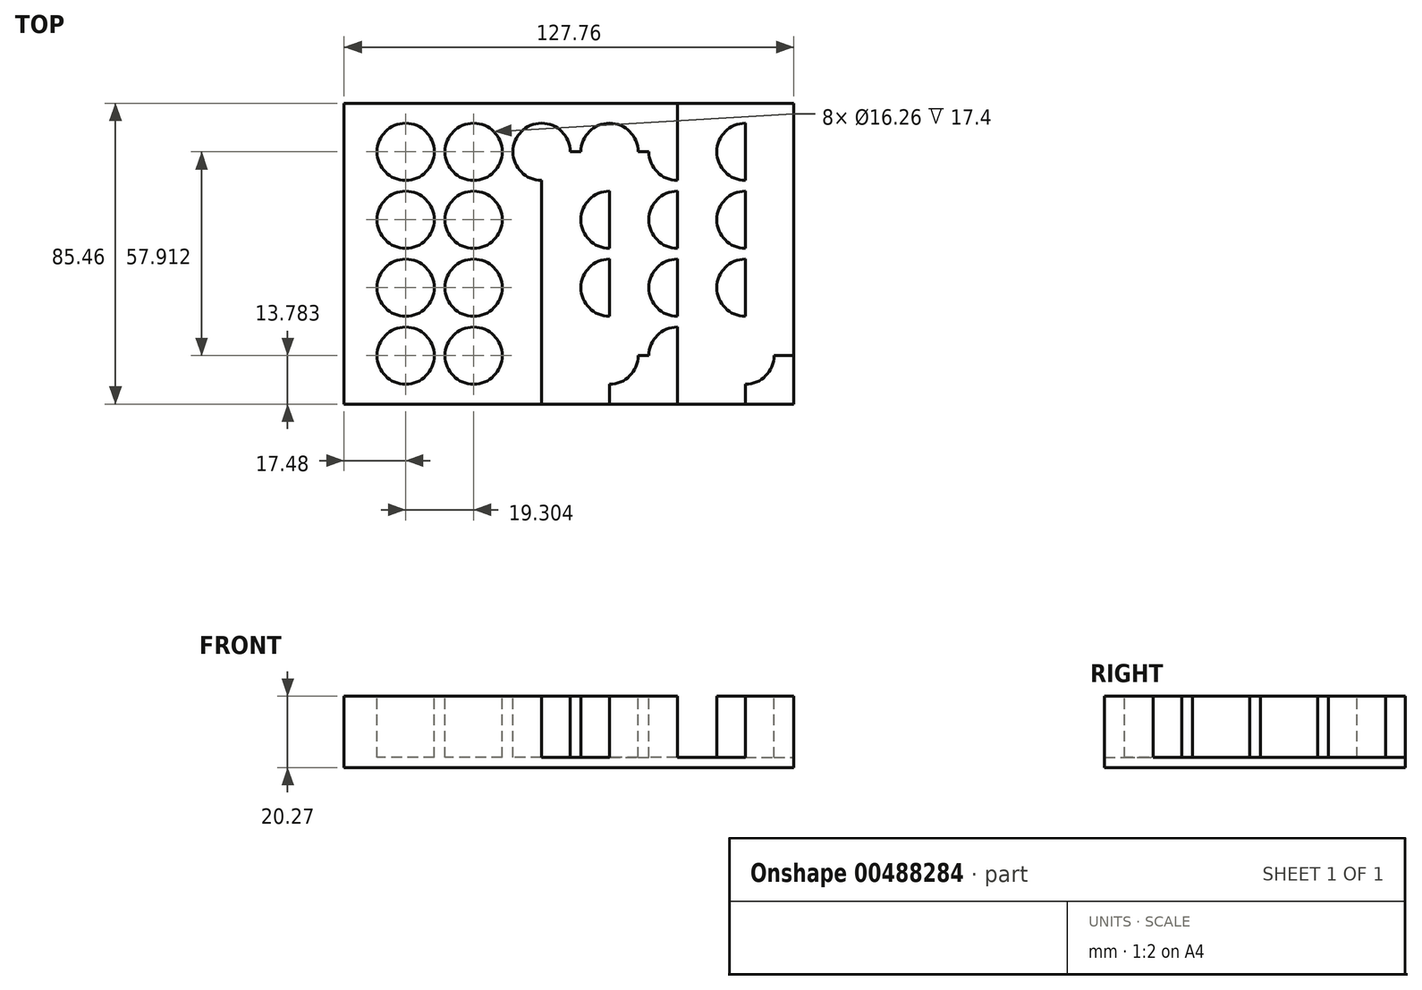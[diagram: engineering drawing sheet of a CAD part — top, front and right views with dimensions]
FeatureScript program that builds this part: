
annotation { "Feature Type Name" : "Feature", "Feature Type Description" : "" }
export const myFeature = defineFeature(function(context is Context, id is Id, definition is map)
    precondition{}
    {
        {
            var Q0;
            Q0=qCreatedBy(makeId("Top.planeOp"),FACE);
            var sketch = newSketch(context, id + "F0", { "sketchPlane" : qUnion([Q0])});
            skLineSegment(sketch, "E0.bottom", {"start": v(63.88, 42.73) * mm, "end": v(-63.88, 42.73) * mm});
            skLineSegment(sketch, "E0.top", {"start": v(63.88, -42.73) * mm, "end": v(-63.88, -42.73) * mm});
            skLineSegment(sketch, "E0.left", {"start": v(63.88, 42.74) * mm, "end": v(63.88, -42.73) * mm});
            skLineSegment(sketch, "E0.right", {"start": v(-63.88, 42.73) * mm, "end": v(-63.88, -42.73) * mm});
            skPoint(sketch, "E0.middle", {"position": v(0, 0) * mm});
            skSolve(sketch);
        }
        {
            var Q0;
            Q0 = qSketchRegion(id + "F0", true);
            extrude(context, id + "F1", {"entities" : qUnion([Q0]), "depth" : 20.27 * mm, "offsetDistance" : 25 * mm});
        }
        {
            var Q0;
            Q0=makeQuery(id+"F1.opExtrude","CAP_FACE",FACE,{"disambiguationData":[OSD([sQuery(id+"F0.wireOp",EDGE,"E0.bottom"),sQuery(id+"F0.wireOp",EDGE,"E0.top"),sQuery(id+"F0.wireOp",EDGE,"E0.left"),sQuery(id+"F0.wireOp",EDGE,"E0.right")])],"isStart":false});
            var sketch = newSketch(context, id + "F2", { "sketchPlane" : qUnion([Q0])});
            skLineSegment(sketch, "E1.bottom", {"start": v(63.88, 42.73) * mm, "end": v(-63.88, 42.73) * mm});
            skLineSegment(sketch, "E1.top", {"start": v(63.88, -42.73) * mm, "end": v(-63.88, -42.73) * mm});
            skLineSegment(sketch, "E1.left", {"start": v(63.88, 42.73) * mm, "end": v(63.88, -42.73) * mm});
            skLineSegment(sketch, "E1.right", {"start": v(-63.88, 42.73) * mm, "end": v(-63.88, -42.74) * mm});
            skPoint(sketch, "E1.middle", {"position": v(0, 0) * mm});
            skLineSegment(sketch, "E2", {"start": v(-63.88, -42.73) * mm, "end": v(-46.4, -42.73) * mm});
            skLineSegment(sketch, "E3", {"start": v(-63.88, 42.73) * mm, "end": v(-63.88, 28.96) * mm});
            skLineSegment(sketch, "E4", {"start": v(-46.4, -42.73) * mm, "end": v(-27.1, -42.73) * mm});
            skLineSegment(sketch, "E5", {"start": v(-27.1, -42.73) * mm, "end": v(-7.8, -42.73) * mm});
            skLineSegment(sketch, "E6", {"start": v(-7.8, -42.73) * mm, "end": v(11.51, -42.73) * mm});
            skLineSegment(sketch, "E7", {"start": v(11.51, -42.73) * mm, "end": v(30.82, -42.73) * mm});
            skLineSegment(sketch, "E8", {"start": v(30.82, -42.73) * mm, "end": v(50.12, -42.73) * mm});
            skLineSegment(sketch, "E9", {"start": v(50.12, -42.73) * mm, "end": v(63.88, -42.73) * mm});
            skLineSegment(sketch, "E10", {"start": v(-63.88, 28.96) * mm, "end": v(-63.88, 9.66) * mm});
            skLineSegment(sketch, "E11", {"start": v(-63.88, 9.66) * mm, "end": v(-63.88, -9.64) * mm});
            skLineSegment(sketch, "E12", {"start": v(-63.88, -9.64) * mm, "end": v(-63.88, -28.95) * mm});
            skLineSegment(sketch, "E13", {"start": v(-63.88, -28.95) * mm, "end": v(-63.88, -42.73) * mm});
            skLineSegment(sketch, "E14", {"start": v(-63.88, 28.96) * mm, "end": v(63.88, 28.96) * mm});
            skLineSegment(sketch, "E15", {"start": v(63.88, 28.96) * mm, "end": v(63.88, 42.73) * mm});
            skLineSegment(sketch, "E16", {"start": v(-63.88, 9.66) * mm, "end": v(63.88, 9.66) * mm});
            skLineSegment(sketch, "E17", {"start": v(63.88, 9.66) * mm, "end": v(63.88, 28.96) * mm});
            skLineSegment(sketch, "E18", {"start": v(-63.88, -9.64) * mm, "end": v(63.88, -9.64) * mm});
            skLineSegment(sketch, "E19", {"start": v(63.88, -9.64) * mm, "end": v(63.88, 9.66) * mm});
            skLineSegment(sketch, "E20", {"start": v(-63.88, -28.95) * mm, "end": v(63.88, -28.95) * mm});
            skLineSegment(sketch, "E21", {"start": v(63.88, -28.95) * mm, "end": v(63.88, -9.64) * mm});
            skLineSegment(sketch, "E22", {"start": v(-46.4, -42.73) * mm, "end": v(-46.4, 42.73) * mm});
            skLineSegment(sketch, "E23", {"start": v(-46.4, 42.73) * mm, "end": v(-63.88, 42.73) * mm});
            skLineSegment(sketch, "E24", {"start": v(-27.1, -42.73) * mm, "end": v(-27.1, 42.73) * mm});
            skLineSegment(sketch, "E25", {"start": v(-27.1, 42.73) * mm, "end": v(-46.4, 42.73) * mm});
            skLineSegment(sketch, "E26", {"start": v(-7.8, -42.73) * mm, "end": v(-7.8, 42.73) * mm});
            skLineSegment(sketch, "E27", {"start": v(-7.8, 42.73) * mm, "end": v(-27.1, 42.73) * mm});
            skLineSegment(sketch, "E28", {"start": v(11.51, -42.73) * mm, "end": v(11.51, 42.73) * mm});
            skLineSegment(sketch, "E29", {"start": v(11.51, 42.73) * mm, "end": v(-7.8, 42.73) * mm});
            skLineSegment(sketch, "E30", {"start": v(30.82, -42.73) * mm, "end": v(30.82, 42.73) * mm});
            skLineSegment(sketch, "E31", {"start": v(30.82, 42.73) * mm, "end": v(11.51, 42.73) * mm});
            skLineSegment(sketch, "E32", {"start": v(50.12, -42.73) * mm, "end": v(50.12, 42.73) * mm});
            skLineSegment(sketch, "E33", {"start": v(50.12, 42.73) * mm, "end": v(30.82, 42.73) * mm});
            skLineSegment(sketch, "E34", {"start": v(50.12, 42.73) * mm, "end": v(63.88, 42.73) * mm});
            skLineSegment(sketch, "E35", {"start": v(63.88, -28.95) * mm, "end": v(63.88, -42.73) * mm});
            skCircle(sketch, "E36", {"center": v(-46.4, 28.96) * mm, "radius": 8.13 * mm});
            skCircle(sketch, "E37", {"center": v(-27.1, 28.96) * mm, "radius": 8.13 * mm});
            skCircle(sketch, "E38", {"center": v(-7.8, 28.96) * mm, "radius": 8.13 * mm});
            skCircle(sketch, "E39", {"center": v(11.51, 28.96) * mm, "radius": 8.13 * mm});
            skCircle(sketch, "E40", {"center": v(30.82, 28.96) * mm, "radius": 8.13 * mm});
            skCircle(sketch, "E41", {"center": v(50.12, 28.97) * mm, "radius": 8.13 * mm});
            skCircle(sketch, "E42", {"center": v(-27.1, 9.66) * mm, "radius": 8.13 * mm});
            skCircle(sketch, "E43", {"center": v(-7.8, 9.66) * mm, "radius": 8.13 * mm});
            skCircle(sketch, "E44", {"center": v(11.51, 9.66) * mm, "radius": 8.13 * mm});
            skCircle(sketch, "E45", {"center": v(30.82, 9.66) * mm, "radius": 8.13 * mm});
            skCircle(sketch, "E46", {"center": v(50.12, 9.66) * mm, "radius": 8.13 * mm});
            skCircle(sketch, "E47", {"center": v(-27.1, -9.64) * mm, "radius": 8.13 * mm});
            skCircle(sketch, "E48", {"center": v(-7.8, -9.64) * mm, "radius": 8.13 * mm});
            skCircle(sketch, "E49", {"center": v(11.51, -9.64) * mm, "radius": 8.13 * mm});
            skCircle(sketch, "E50", {"center": v(30.82, -9.64) * mm, "radius": 8.13 * mm});
            skCircle(sketch, "E51", {"center": v(50.12, -9.64) * mm, "radius": 8.13 * mm});
            skCircle(sketch, "E52", {"center": v(-27.1, -28.95) * mm, "radius": 8.13 * mm});
            skCircle(sketch, "E53", {"center": v(-7.8, -28.95) * mm, "radius": 8.13 * mm});
            skCircle(sketch, "E54", {"center": v(11.51, -28.95) * mm, "radius": 8.13 * mm});
            skCircle(sketch, "E55", {"center": v(30.82, -28.95) * mm, "radius": 8.13 * mm});
            skCircle(sketch, "E56", {"center": v(50.12, -28.95) * mm, "radius": 8.13 * mm});
            skCircle(sketch, "E57", {"center": v(-46.4, 9.66) * mm, "radius": 8.13 * mm});
            skCircle(sketch, "E58", {"center": v(-46.4, -9.64) * mm, "radius": 8.13 * mm});
            skCircle(sketch, "E59", {"center": v(-46.4, -28.95) * mm, "radius": 8.13 * mm});
            skCircle(sketch, "E60", {"center": v(0, 0) * mm, "radius": 0.5 * mm});
            skSolve(sketch);
        }
        {
            var Q0;
            {var subQ0=sQuery(id+"F2.wireOp",EDGE,"E36");var subQ1=sQuery(id+"F2.wireOp",EDGE,"E14");var subQ2=makeQuery(id+"F2.imprint","INTERSECT",VERTEX,{"disambiguationData":[OD(0.0)],"derivedFrom":[subQ1,subQ0]});Q0=makeQuery(id+"F2.imprint","IMPRINT",FACE,{"disambiguationData":[TD([[makeQuery(id+"F2.imprint","IMPRINT",EDGE,{"disambiguationData":[TD([[subQ2,-1.0]])],"derivedFrom":subQ1}),1.0]])]});}
            var Q1;
            {var subQ0=sQuery(id+"F2.wireOp",EDGE,"E22");var subQ1=sQuery(id+"F2.wireOp",EDGE,"E14");var subQ2=makeQuery(id+"F2.imprint","INTERSECT",VERTEX,{"derivedFrom":[subQ1,subQ0]});Q1=makeQuery(id+"F2.imprint","IMPRINT",FACE,{"disambiguationData":[TD([[makeQuery(id+"F2.imprint","IMPRINT",EDGE,{"disambiguationData":[TD([[subQ2,-1.0]])],"derivedFrom":subQ1}),1.0]])]});}
            var Q2;
            {var subQ0=sQuery(id+"F2.wireOp",EDGE,"E36");var subQ1=sQuery(id+"F2.wireOp",EDGE,"E14");var subQ2=makeQuery(id+"F2.imprint","INTERSECT",VERTEX,{"disambiguationData":[OD(0.0)],"derivedFrom":[subQ1,subQ0]});Q2=makeQuery(id+"F2.imprint","IMPRINT",FACE,{"disambiguationData":[TD([[makeQuery(id+"F2.imprint","IMPRINT",EDGE,{"disambiguationData":[TD([[subQ2,-1.0]])],"derivedFrom":subQ1}),-1.0]])]});}
            var Q3;
            {var subQ0=sQuery(id+"F2.wireOp",EDGE,"E22");var subQ1=sQuery(id+"F2.wireOp",EDGE,"E14");var subQ2=makeQuery(id+"F2.imprint","INTERSECT",VERTEX,{"derivedFrom":[subQ1,subQ0]});Q3=makeQuery(id+"F2.imprint","IMPRINT",FACE,{"disambiguationData":[TD([[makeQuery(id+"F2.imprint","IMPRINT",EDGE,{"disambiguationData":[TD([[subQ2,-1.0]])],"derivedFrom":subQ1}),-1.0]])]});}
            var Q4;
            {var subQ0=sQuery(id+"F2.wireOp",EDGE,"E37");var subQ1=sQuery(id+"F2.wireOp",EDGE,"E14");var subQ2=makeQuery(id+"F2.imprint","INTERSECT",VERTEX,{"disambiguationData":[OD(0.0)],"derivedFrom":[subQ1,subQ0]});Q4=makeQuery(id+"F2.imprint","IMPRINT",FACE,{"disambiguationData":[TD([[makeQuery(id+"F2.imprint","IMPRINT",EDGE,{"disambiguationData":[TD([[subQ2,-1.0]])],"derivedFrom":subQ1}),1.0]])]});}
            var Q5;
            {var subQ0=sQuery(id+"F2.wireOp",EDGE,"E24");var subQ1=sQuery(id+"F2.wireOp",EDGE,"E14");var subQ2=makeQuery(id+"F2.imprint","INTERSECT",VERTEX,{"derivedFrom":[subQ1,subQ0]});Q5=makeQuery(id+"F2.imprint","IMPRINT",FACE,{"disambiguationData":[TD([[makeQuery(id+"F2.imprint","IMPRINT",EDGE,{"disambiguationData":[TD([[subQ2,-1.0]])],"derivedFrom":subQ1}),1.0]])]});}
            var Q6;
            {var subQ0=sQuery(id+"F2.wireOp",EDGE,"E37");var subQ1=sQuery(id+"F2.wireOp",EDGE,"E14");var subQ2=makeQuery(id+"F2.imprint","INTERSECT",VERTEX,{"disambiguationData":[OD(0.0)],"derivedFrom":[subQ1,subQ0]});Q6=makeQuery(id+"F2.imprint","IMPRINT",FACE,{"disambiguationData":[TD([[makeQuery(id+"F2.imprint","IMPRINT",EDGE,{"disambiguationData":[TD([[subQ2,-1.0]])],"derivedFrom":subQ1}),-1.0]])]});}
            var Q7;
            {var subQ0=sQuery(id+"F2.wireOp",EDGE,"E24");var subQ1=sQuery(id+"F2.wireOp",EDGE,"E14");var subQ2=makeQuery(id+"F2.imprint","INTERSECT",VERTEX,{"derivedFrom":[subQ1,subQ0]});Q7=makeQuery(id+"F2.imprint","IMPRINT",FACE,{"disambiguationData":[TD([[makeQuery(id+"F2.imprint","IMPRINT",EDGE,{"disambiguationData":[TD([[subQ2,-1.0]])],"derivedFrom":subQ1}),-1.0]])]});}
            var Q8;
            {var subQ0=sQuery(id+"F2.wireOp",EDGE,"E57");var subQ1=sQuery(id+"F2.wireOp",EDGE,"E16");var subQ2=makeQuery(id+"F2.imprint","INTERSECT",VERTEX,{"disambiguationData":[OD(0.0)],"derivedFrom":[subQ1,subQ0]});Q8=makeQuery(id+"F2.imprint","IMPRINT",FACE,{"disambiguationData":[TD([[makeQuery(id+"F2.imprint","IMPRINT",EDGE,{"disambiguationData":[TD([[subQ2,-1.0]])],"derivedFrom":subQ1}),1.0]])]});}
            var Q9;
            {var subQ0=sQuery(id+"F2.wireOp",EDGE,"E22");var subQ1=sQuery(id+"F2.wireOp",EDGE,"E16");var subQ2=makeQuery(id+"F2.imprint","INTERSECT",VERTEX,{"derivedFrom":[subQ1,subQ0]});Q9=makeQuery(id+"F2.imprint","IMPRINT",FACE,{"disambiguationData":[TD([[makeQuery(id+"F2.imprint","IMPRINT",EDGE,{"disambiguationData":[TD([[subQ2,-1.0]])],"derivedFrom":subQ1}),1.0]])]});}
            var Q10;
            {var subQ0=sQuery(id+"F2.wireOp",EDGE,"E57");var subQ1=sQuery(id+"F2.wireOp",EDGE,"E16");var subQ2=makeQuery(id+"F2.imprint","INTERSECT",VERTEX,{"disambiguationData":[OD(0.0)],"derivedFrom":[subQ1,subQ0]});Q10=makeQuery(id+"F2.imprint","IMPRINT",FACE,{"disambiguationData":[TD([[makeQuery(id+"F2.imprint","IMPRINT",EDGE,{"disambiguationData":[TD([[subQ2,-1.0]])],"derivedFrom":subQ1}),-1.0]])]});}
            var Q11;
            {var subQ0=sQuery(id+"F2.wireOp",EDGE,"E22");var subQ1=sQuery(id+"F2.wireOp",EDGE,"E16");var subQ2=makeQuery(id+"F2.imprint","INTERSECT",VERTEX,{"derivedFrom":[subQ1,subQ0]});Q11=makeQuery(id+"F2.imprint","IMPRINT",FACE,{"disambiguationData":[TD([[makeQuery(id+"F2.imprint","IMPRINT",EDGE,{"disambiguationData":[TD([[subQ2,-1.0]])],"derivedFrom":subQ1}),-1.0]])]});}
            var Q12;
            {var subQ0=sQuery(id+"F2.wireOp",EDGE,"E42");var subQ1=sQuery(id+"F2.wireOp",EDGE,"E16");var subQ2=makeQuery(id+"F2.imprint","INTERSECT",VERTEX,{"disambiguationData":[OD(0.0)],"derivedFrom":[subQ1,subQ0]});Q12=makeQuery(id+"F2.imprint","IMPRINT",FACE,{"disambiguationData":[TD([[makeQuery(id+"F2.imprint","IMPRINT",EDGE,{"disambiguationData":[TD([[subQ2,-1.0]])],"derivedFrom":subQ1}),1.0]])]});}
            var Q13;
            {var subQ0=sQuery(id+"F2.wireOp",EDGE,"E24");var subQ1=sQuery(id+"F2.wireOp",EDGE,"E16");var subQ2=makeQuery(id+"F2.imprint","INTERSECT",VERTEX,{"derivedFrom":[subQ1,subQ0]});Q13=makeQuery(id+"F2.imprint","IMPRINT",FACE,{"disambiguationData":[TD([[makeQuery(id+"F2.imprint","IMPRINT",EDGE,{"disambiguationData":[TD([[subQ2,-1.0]])],"derivedFrom":subQ1}),1.0]])]});}
            var Q14;
            {var subQ0=sQuery(id+"F2.wireOp",EDGE,"E42");var subQ1=sQuery(id+"F2.wireOp",EDGE,"E16");var subQ2=makeQuery(id+"F2.imprint","INTERSECT",VERTEX,{"disambiguationData":[OD(0.0)],"derivedFrom":[subQ1,subQ0]});Q14=makeQuery(id+"F2.imprint","IMPRINT",FACE,{"disambiguationData":[TD([[makeQuery(id+"F2.imprint","IMPRINT",EDGE,{"disambiguationData":[TD([[subQ2,-1.0]])],"derivedFrom":subQ1}),-1.0]])]});}
            var Q15;
            {var subQ0=sQuery(id+"F2.wireOp",EDGE,"E24");var subQ1=sQuery(id+"F2.wireOp",EDGE,"E16");var subQ2=makeQuery(id+"F2.imprint","INTERSECT",VERTEX,{"derivedFrom":[subQ1,subQ0]});Q15=makeQuery(id+"F2.imprint","IMPRINT",FACE,{"disambiguationData":[TD([[makeQuery(id+"F2.imprint","IMPRINT",EDGE,{"disambiguationData":[TD([[subQ2,-1.0]])],"derivedFrom":subQ1}),-1.0]])]});}
            var Q16;
            {var subQ0=sQuery(id+"F2.wireOp",EDGE,"E22");var subQ1=sQuery(id+"F2.wireOp",EDGE,"E18");var subQ2=makeQuery(id+"F2.imprint","INTERSECT",VERTEX,{"derivedFrom":[subQ1,subQ0]});Q16=makeQuery(id+"F2.imprint","IMPRINT",FACE,{"disambiguationData":[TD([[makeQuery(id+"F2.imprint","IMPRINT",EDGE,{"disambiguationData":[TD([[subQ2,-1.0]])],"derivedFrom":subQ1}),1.0]])]});}
            var Q17;
            {var subQ0=sQuery(id+"F2.wireOp",EDGE,"E58");var subQ1=sQuery(id+"F2.wireOp",EDGE,"E18");var subQ2=makeQuery(id+"F2.imprint","INTERSECT",VERTEX,{"disambiguationData":[OD(0.0)],"derivedFrom":[subQ1,subQ0]});Q17=makeQuery(id+"F2.imprint","IMPRINT",FACE,{"disambiguationData":[TD([[makeQuery(id+"F2.imprint","IMPRINT",EDGE,{"disambiguationData":[TD([[subQ2,-1.0]])],"derivedFrom":subQ1}),1.0]])]});}
            var Q18;
            {var subQ0=sQuery(id+"F2.wireOp",EDGE,"E58");var subQ1=sQuery(id+"F2.wireOp",EDGE,"E18");var subQ2=makeQuery(id+"F2.imprint","INTERSECT",VERTEX,{"disambiguationData":[OD(0.0)],"derivedFrom":[subQ1,subQ0]});Q18=makeQuery(id+"F2.imprint","IMPRINT",FACE,{"disambiguationData":[TD([[makeQuery(id+"F2.imprint","IMPRINT",EDGE,{"disambiguationData":[TD([[subQ2,-1.0]])],"derivedFrom":subQ1}),-1.0]])]});}
            var Q19;
            {var subQ0=sQuery(id+"F2.wireOp",EDGE,"E22");var subQ1=sQuery(id+"F2.wireOp",EDGE,"E18");var subQ2=makeQuery(id+"F2.imprint","INTERSECT",VERTEX,{"derivedFrom":[subQ1,subQ0]});Q19=makeQuery(id+"F2.imprint","IMPRINT",FACE,{"disambiguationData":[TD([[makeQuery(id+"F2.imprint","IMPRINT",EDGE,{"disambiguationData":[TD([[subQ2,-1.0]])],"derivedFrom":subQ1}),-1.0]])]});}
            var Q20;
            {var subQ0=sQuery(id+"F2.wireOp",EDGE,"E59");var subQ1=sQuery(id+"F2.wireOp",EDGE,"E20");var subQ2=makeQuery(id+"F2.imprint","INTERSECT",VERTEX,{"disambiguationData":[OD(0.0)],"derivedFrom":[subQ1,subQ0]});Q20=makeQuery(id+"F2.imprint","IMPRINT",FACE,{"disambiguationData":[TD([[makeQuery(id+"F2.imprint","IMPRINT",EDGE,{"disambiguationData":[TD([[subQ2,-1.0]])],"derivedFrom":subQ1}),1.0]])]});}
            var Q21;
            {var subQ0=sQuery(id+"F2.wireOp",EDGE,"E22");var subQ1=sQuery(id+"F2.wireOp",EDGE,"E20");var subQ2=makeQuery(id+"F2.imprint","INTERSECT",VERTEX,{"derivedFrom":[subQ1,subQ0]});Q21=makeQuery(id+"F2.imprint","IMPRINT",FACE,{"disambiguationData":[TD([[makeQuery(id+"F2.imprint","IMPRINT",EDGE,{"disambiguationData":[TD([[subQ2,-1.0]])],"derivedFrom":subQ1}),1.0]])]});}
            var Q22;
            {var subQ0=sQuery(id+"F2.wireOp",EDGE,"E59");var subQ1=sQuery(id+"F2.wireOp",EDGE,"E20");var subQ2=makeQuery(id+"F2.imprint","INTERSECT",VERTEX,{"disambiguationData":[OD(0.0)],"derivedFrom":[subQ1,subQ0]});Q22=makeQuery(id+"F2.imprint","IMPRINT",FACE,{"disambiguationData":[TD([[makeQuery(id+"F2.imprint","IMPRINT",EDGE,{"disambiguationData":[TD([[subQ2,-1.0]])],"derivedFrom":subQ1}),-1.0]])]});}
            var Q23;
            {var subQ0=sQuery(id+"F2.wireOp",EDGE,"E22");var subQ1=sQuery(id+"F2.wireOp",EDGE,"E20");var subQ2=makeQuery(id+"F2.imprint","INTERSECT",VERTEX,{"derivedFrom":[subQ1,subQ0]});Q23=makeQuery(id+"F2.imprint","IMPRINT",FACE,{"disambiguationData":[TD([[makeQuery(id+"F2.imprint","IMPRINT",EDGE,{"disambiguationData":[TD([[subQ2,-1.0]])],"derivedFrom":subQ1}),-1.0]])]});}
            var Q24;
            {var subQ0=sQuery(id+"F2.wireOp",EDGE,"E52");var subQ1=sQuery(id+"F2.wireOp",EDGE,"E20");var subQ2=makeQuery(id+"F2.imprint","INTERSECT",VERTEX,{"disambiguationData":[OD(0.0)],"derivedFrom":[subQ1,subQ0]});Q24=makeQuery(id+"F2.imprint","IMPRINT",FACE,{"disambiguationData":[TD([[makeQuery(id+"F2.imprint","IMPRINT",EDGE,{"disambiguationData":[TD([[subQ2,-1.0]])],"derivedFrom":subQ1}),-1.0]])]});}
            var Q25;
            {var subQ0=sQuery(id+"F2.wireOp",EDGE,"E24");var subQ1=sQuery(id+"F2.wireOp",EDGE,"E20");var subQ2=makeQuery(id+"F2.imprint","INTERSECT",VERTEX,{"derivedFrom":[subQ1,subQ0]});Q25=makeQuery(id+"F2.imprint","IMPRINT",FACE,{"disambiguationData":[TD([[makeQuery(id+"F2.imprint","IMPRINT",EDGE,{"disambiguationData":[TD([[subQ2,-1.0]])],"derivedFrom":subQ1}),-1.0]])]});}
            var Q26;
            {var subQ0=sQuery(id+"F2.wireOp",EDGE,"E24");var subQ1=sQuery(id+"F2.wireOp",EDGE,"E20");var subQ2=makeQuery(id+"F2.imprint","INTERSECT",VERTEX,{"derivedFrom":[subQ1,subQ0]});Q26=makeQuery(id+"F2.imprint","IMPRINT",FACE,{"disambiguationData":[TD([[makeQuery(id+"F2.imprint","IMPRINT",EDGE,{"disambiguationData":[TD([[subQ2,-1.0]])],"derivedFrom":subQ1}),1.0]])]});}
            var Q27;
            {var subQ0=sQuery(id+"F2.wireOp",EDGE,"E52");var subQ1=sQuery(id+"F2.wireOp",EDGE,"E20");var subQ2=makeQuery(id+"F2.imprint","INTERSECT",VERTEX,{"disambiguationData":[OD(0.0)],"derivedFrom":[subQ1,subQ0]});Q27=makeQuery(id+"F2.imprint","IMPRINT",FACE,{"disambiguationData":[TD([[makeQuery(id+"F2.imprint","IMPRINT",EDGE,{"disambiguationData":[TD([[subQ2,-1.0]])],"derivedFrom":subQ1}),1.0]])]});}
            var Q28;
            {var subQ0=sQuery(id+"F2.wireOp",EDGE,"E47");var subQ1=sQuery(id+"F2.wireOp",EDGE,"E18");var subQ2=makeQuery(id+"F2.imprint","INTERSECT",VERTEX,{"disambiguationData":[OD(0.0)],"derivedFrom":[subQ1,subQ0]});Q28=makeQuery(id+"F2.imprint","IMPRINT",FACE,{"disambiguationData":[TD([[makeQuery(id+"F2.imprint","IMPRINT",EDGE,{"disambiguationData":[TD([[subQ2,-1.0]])],"derivedFrom":subQ1}),-1.0]])]});}
            var Q29;
            {var subQ0=sQuery(id+"F2.wireOp",EDGE,"E24");var subQ1=sQuery(id+"F2.wireOp",EDGE,"E18");var subQ2=makeQuery(id+"F2.imprint","INTERSECT",VERTEX,{"derivedFrom":[subQ1,subQ0]});Q29=makeQuery(id+"F2.imprint","IMPRINT",FACE,{"disambiguationData":[TD([[makeQuery(id+"F2.imprint","IMPRINT",EDGE,{"disambiguationData":[TD([[subQ2,-1.0]])],"derivedFrom":subQ1}),-1.0]])]});}
            var Q30;
            {var subQ0=sQuery(id+"F2.wireOp",EDGE,"E24");var subQ1=sQuery(id+"F2.wireOp",EDGE,"E18");var subQ2=makeQuery(id+"F2.imprint","INTERSECT",VERTEX,{"derivedFrom":[subQ1,subQ0]});Q30=makeQuery(id+"F2.imprint","IMPRINT",FACE,{"disambiguationData":[TD([[makeQuery(id+"F2.imprint","IMPRINT",EDGE,{"disambiguationData":[TD([[subQ2,-1.0]])],"derivedFrom":subQ1}),1.0]])]});}
            var Q31;
            {var subQ0=sQuery(id+"F2.wireOp",EDGE,"E47");var subQ1=sQuery(id+"F2.wireOp",EDGE,"E18");var subQ2=makeQuery(id+"F2.imprint","INTERSECT",VERTEX,{"disambiguationData":[OD(0.0)],"derivedFrom":[subQ1,subQ0]});Q31=makeQuery(id+"F2.imprint","IMPRINT",FACE,{"disambiguationData":[TD([[makeQuery(id+"F2.imprint","IMPRINT",EDGE,{"disambiguationData":[TD([[subQ2,-1.0]])],"derivedFrom":subQ1}),1.0]])]});}
            var Q32;
            {var subQ0=sQuery(id+"F2.wireOp",EDGE,"E43");var subQ1=sQuery(id+"F2.wireOp",EDGE,"E16");var subQ2=makeQuery(id+"F2.imprint","INTERSECT",VERTEX,{"disambiguationData":[OD(0.0)],"derivedFrom":[subQ1,subQ0]});Q32=makeQuery(id+"F2.imprint","IMPRINT",FACE,{"disambiguationData":[TD([[makeQuery(id+"F2.imprint","IMPRINT",EDGE,{"disambiguationData":[TD([[subQ2,-1.0]])],"derivedFrom":subQ1}),-1.0]])]});}
            var Q33;
            {var subQ0=sQuery(id+"F2.wireOp",EDGE,"E26");var subQ1=sQuery(id+"F2.wireOp",EDGE,"E16");var subQ2=makeQuery(id+"F2.imprint","INTERSECT",VERTEX,{"derivedFrom":[subQ1,subQ0]});Q33=makeQuery(id+"F2.imprint","IMPRINT",FACE,{"disambiguationData":[TD([[makeQuery(id+"F2.imprint","IMPRINT",EDGE,{"disambiguationData":[TD([[subQ2,-1.0]])],"derivedFrom":subQ1}),-1.0]])]});}
            var Q34;
            {var subQ0=sQuery(id+"F2.wireOp",EDGE,"E26");var subQ1=sQuery(id+"F2.wireOp",EDGE,"E16");var subQ2=makeQuery(id+"F2.imprint","INTERSECT",VERTEX,{"derivedFrom":[subQ1,subQ0]});Q34=makeQuery(id+"F2.imprint","IMPRINT",FACE,{"disambiguationData":[TD([[makeQuery(id+"F2.imprint","IMPRINT",EDGE,{"disambiguationData":[TD([[subQ2,-1.0]])],"derivedFrom":subQ1}),1.0]])]});}
            var Q35;
            {var subQ0=sQuery(id+"F2.wireOp",EDGE,"E43");var subQ1=sQuery(id+"F2.wireOp",EDGE,"E16");var subQ2=makeQuery(id+"F2.imprint","INTERSECT",VERTEX,{"disambiguationData":[OD(0.0)],"derivedFrom":[subQ1,subQ0]});Q35=makeQuery(id+"F2.imprint","IMPRINT",FACE,{"disambiguationData":[TD([[makeQuery(id+"F2.imprint","IMPRINT",EDGE,{"disambiguationData":[TD([[subQ2,-1.0]])],"derivedFrom":subQ1}),1.0]])]});}
            var Q36;
            {var subQ0=sQuery(id+"F2.wireOp",EDGE,"E38");var subQ1=sQuery(id+"F2.wireOp",EDGE,"E14");var subQ2=makeQuery(id+"F2.imprint","INTERSECT",VERTEX,{"disambiguationData":[OD(0.0)],"derivedFrom":[subQ1,subQ0]});Q36=makeQuery(id+"F2.imprint","IMPRINT",FACE,{"disambiguationData":[TD([[makeQuery(id+"F2.imprint","IMPRINT",EDGE,{"disambiguationData":[TD([[subQ2,-1.0]])],"derivedFrom":subQ1}),-1.0]])]});}
            var Q37;
            {var subQ0=sQuery(id+"F2.wireOp",EDGE,"E26");var subQ1=sQuery(id+"F2.wireOp",EDGE,"E14");var subQ2=makeQuery(id+"F2.imprint","INTERSECT",VERTEX,{"derivedFrom":[subQ1,subQ0]});Q37=makeQuery(id+"F2.imprint","IMPRINT",FACE,{"disambiguationData":[TD([[makeQuery(id+"F2.imprint","IMPRINT",EDGE,{"disambiguationData":[TD([[subQ2,-1.0]])],"derivedFrom":subQ1}),-1.0]])]});}
            var Q38;
            {var subQ0=sQuery(id+"F2.wireOp",EDGE,"E26");var subQ1=sQuery(id+"F2.wireOp",EDGE,"E14");var subQ2=makeQuery(id+"F2.imprint","INTERSECT",VERTEX,{"derivedFrom":[subQ1,subQ0]});Q38=makeQuery(id+"F2.imprint","IMPRINT",FACE,{"disambiguationData":[TD([[makeQuery(id+"F2.imprint","IMPRINT",EDGE,{"disambiguationData":[TD([[subQ2,-1.0]])],"derivedFrom":subQ1}),1.0]])]});}
            var Q39;
            {var subQ0=sQuery(id+"F2.wireOp",EDGE,"E38");var subQ1=sQuery(id+"F2.wireOp",EDGE,"E14");var subQ2=makeQuery(id+"F2.imprint","INTERSECT",VERTEX,{"disambiguationData":[OD(0.0)],"derivedFrom":[subQ1,subQ0]});Q39=makeQuery(id+"F2.imprint","IMPRINT",FACE,{"disambiguationData":[TD([[makeQuery(id+"F2.imprint","IMPRINT",EDGE,{"disambiguationData":[TD([[subQ2,-1.0]])],"derivedFrom":subQ1}),1.0]])]});}
            var Q40;
            {var subQ0=sQuery(id+"F2.wireOp",EDGE,"E39");var subQ1=sQuery(id+"F2.wireOp",EDGE,"E14");var subQ2=makeQuery(id+"F2.imprint","INTERSECT",VERTEX,{"disambiguationData":[OD(0.0)],"derivedFrom":[subQ1,subQ0]});Q40=makeQuery(id+"F2.imprint","IMPRINT",FACE,{"disambiguationData":[TD([[makeQuery(id+"F2.imprint","IMPRINT",EDGE,{"disambiguationData":[TD([[subQ2,-1.0]])],"derivedFrom":subQ1}),1.0]])]});}
            var Q41;
            {var subQ0=sQuery(id+"F2.wireOp",EDGE,"E28");var subQ1=sQuery(id+"F2.wireOp",EDGE,"E14");var subQ2=makeQuery(id+"F2.imprint","INTERSECT",VERTEX,{"derivedFrom":[subQ1,subQ0]});Q41=makeQuery(id+"F2.imprint","IMPRINT",FACE,{"disambiguationData":[TD([[makeQuery(id+"F2.imprint","IMPRINT",EDGE,{"disambiguationData":[TD([[subQ2,-1.0]])],"derivedFrom":subQ1}),1.0]])]});}
            var Q42;
            {var subQ0=sQuery(id+"F2.wireOp",EDGE,"E28");var subQ1=sQuery(id+"F2.wireOp",EDGE,"E14");var subQ2=makeQuery(id+"F2.imprint","INTERSECT",VERTEX,{"derivedFrom":[subQ1,subQ0]});Q42=makeQuery(id+"F2.imprint","IMPRINT",FACE,{"disambiguationData":[TD([[makeQuery(id+"F2.imprint","IMPRINT",EDGE,{"disambiguationData":[TD([[subQ2,-1.0]])],"derivedFrom":subQ1}),-1.0]])]});}
            var Q43;
            {var subQ0=sQuery(id+"F2.wireOp",EDGE,"E39");var subQ1=sQuery(id+"F2.wireOp",EDGE,"E14");var subQ2=makeQuery(id+"F2.imprint","INTERSECT",VERTEX,{"disambiguationData":[OD(0.0)],"derivedFrom":[subQ1,subQ0]});Q43=makeQuery(id+"F2.imprint","IMPRINT",FACE,{"disambiguationData":[TD([[makeQuery(id+"F2.imprint","IMPRINT",EDGE,{"disambiguationData":[TD([[subQ2,-1.0]])],"derivedFrom":subQ1}),-1.0]])]});}
            var Q44;
            {var subQ0=sQuery(id+"F2.wireOp",EDGE,"E44");var subQ1=sQuery(id+"F2.wireOp",EDGE,"E16");var subQ2=makeQuery(id+"F2.imprint","INTERSECT",VERTEX,{"disambiguationData":[OD(0.0)],"derivedFrom":[subQ1,subQ0]});Q44=makeQuery(id+"F2.imprint","IMPRINT",FACE,{"disambiguationData":[TD([[makeQuery(id+"F2.imprint","IMPRINT",EDGE,{"disambiguationData":[TD([[subQ2,-1.0]])],"derivedFrom":subQ1}),1.0]])]});}
            var Q45;
            {var subQ0=sQuery(id+"F2.wireOp",EDGE,"E28");var subQ1=sQuery(id+"F2.wireOp",EDGE,"E16");var subQ2=makeQuery(id+"F2.imprint","INTERSECT",VERTEX,{"derivedFrom":[subQ1,subQ0]});Q45=makeQuery(id+"F2.imprint","IMPRINT",FACE,{"disambiguationData":[TD([[makeQuery(id+"F2.imprint","IMPRINT",EDGE,{"disambiguationData":[TD([[subQ2,-1.0]])],"derivedFrom":subQ1}),1.0]])]});}
            var Q46;
            {var subQ0=sQuery(id+"F2.wireOp",EDGE,"E28");var subQ1=sQuery(id+"F2.wireOp",EDGE,"E16");var subQ2=makeQuery(id+"F2.imprint","INTERSECT",VERTEX,{"derivedFrom":[subQ1,subQ0]});Q46=makeQuery(id+"F2.imprint","IMPRINT",FACE,{"disambiguationData":[TD([[makeQuery(id+"F2.imprint","IMPRINT",EDGE,{"disambiguationData":[TD([[subQ2,-1.0]])],"derivedFrom":subQ1}),-1.0]])]});}
            var Q47;
            {var subQ0=sQuery(id+"F2.wireOp",EDGE,"E44");var subQ1=sQuery(id+"F2.wireOp",EDGE,"E16");var subQ2=makeQuery(id+"F2.imprint","INTERSECT",VERTEX,{"disambiguationData":[OD(0.0)],"derivedFrom":[subQ1,subQ0]});Q47=makeQuery(id+"F2.imprint","IMPRINT",FACE,{"disambiguationData":[TD([[makeQuery(id+"F2.imprint","IMPRINT",EDGE,{"disambiguationData":[TD([[subQ2,-1.0]])],"derivedFrom":subQ1}),-1.0]])]});}
            var Q48;
            {var subQ0=sQuery(id+"F2.wireOp",EDGE,"E49");var subQ1=sQuery(id+"F2.wireOp",EDGE,"E18");var subQ2=makeQuery(id+"F2.imprint","INTERSECT",VERTEX,{"disambiguationData":[OD(0.0)],"derivedFrom":[subQ1,subQ0]});Q48=makeQuery(id+"F2.imprint","IMPRINT",FACE,{"disambiguationData":[TD([[makeQuery(id+"F2.imprint","IMPRINT",EDGE,{"disambiguationData":[TD([[subQ2,-1.0]])],"derivedFrom":subQ1}),1.0]])]});}
            var Q49;
            {var subQ0=sQuery(id+"F2.wireOp",EDGE,"E28");var subQ1=sQuery(id+"F2.wireOp",EDGE,"E18");var subQ2=makeQuery(id+"F2.imprint","INTERSECT",VERTEX,{"derivedFrom":[subQ1,subQ0]});Q49=makeQuery(id+"F2.imprint","IMPRINT",FACE,{"disambiguationData":[TD([[makeQuery(id+"F2.imprint","IMPRINT",EDGE,{"disambiguationData":[TD([[subQ2,-1.0]])],"derivedFrom":subQ1}),1.0]])]});}
            var Q50;
            {var subQ0=sQuery(id+"F2.wireOp",EDGE,"E28");var subQ1=sQuery(id+"F2.wireOp",EDGE,"E18");var subQ2=makeQuery(id+"F2.imprint","INTERSECT",VERTEX,{"derivedFrom":[subQ1,subQ0]});Q50=makeQuery(id+"F2.imprint","IMPRINT",FACE,{"disambiguationData":[TD([[makeQuery(id+"F2.imprint","IMPRINT",EDGE,{"disambiguationData":[TD([[subQ2,-1.0]])],"derivedFrom":subQ1}),-1.0]])]});}
            var Q51;
            {var subQ0=sQuery(id+"F2.wireOp",EDGE,"E49");var subQ1=sQuery(id+"F2.wireOp",EDGE,"E18");var subQ2=makeQuery(id+"F2.imprint","INTERSECT",VERTEX,{"disambiguationData":[OD(0.0)],"derivedFrom":[subQ1,subQ0]});Q51=makeQuery(id+"F2.imprint","IMPRINT",FACE,{"disambiguationData":[TD([[makeQuery(id+"F2.imprint","IMPRINT",EDGE,{"disambiguationData":[TD([[subQ2,-1.0]])],"derivedFrom":subQ1}),-1.0]])]});}
            var Q52;
            {var subQ0=sQuery(id+"F2.wireOp",EDGE,"E26");var subQ1=sQuery(id+"F2.wireOp",EDGE,"E18");var subQ2=makeQuery(id+"F2.imprint","INTERSECT",VERTEX,{"derivedFrom":[subQ1,subQ0]});Q52=makeQuery(id+"F2.imprint","IMPRINT",FACE,{"disambiguationData":[TD([[makeQuery(id+"F2.imprint","IMPRINT",EDGE,{"disambiguationData":[TD([[subQ2,-1.0]])],"derivedFrom":subQ1}),-1.0]])]});}
            var Q53;
            {var subQ0=sQuery(id+"F2.wireOp",EDGE,"E48");var subQ1=sQuery(id+"F2.wireOp",EDGE,"E18");var subQ2=makeQuery(id+"F2.imprint","INTERSECT",VERTEX,{"disambiguationData":[OD(0.0)],"derivedFrom":[subQ1,subQ0]});Q53=makeQuery(id+"F2.imprint","IMPRINT",FACE,{"disambiguationData":[TD([[makeQuery(id+"F2.imprint","IMPRINT",EDGE,{"disambiguationData":[TD([[subQ2,-1.0]])],"derivedFrom":subQ1}),-1.0]])]});}
            var Q54;
            {var subQ0=sQuery(id+"F2.wireOp",EDGE,"E48");var subQ1=sQuery(id+"F2.wireOp",EDGE,"E18");var subQ2=makeQuery(id+"F2.imprint","INTERSECT",VERTEX,{"disambiguationData":[OD(0.0)],"derivedFrom":[subQ1,subQ0]});Q54=makeQuery(id+"F2.imprint","IMPRINT",FACE,{"disambiguationData":[TD([[makeQuery(id+"F2.imprint","IMPRINT",EDGE,{"disambiguationData":[TD([[subQ2,-1.0]])],"derivedFrom":subQ1}),1.0]])]});}
            var Q55;
            {var subQ0=sQuery(id+"F2.wireOp",EDGE,"E26");var subQ1=sQuery(id+"F2.wireOp",EDGE,"E18");var subQ2=makeQuery(id+"F2.imprint","INTERSECT",VERTEX,{"derivedFrom":[subQ1,subQ0]});Q55=makeQuery(id+"F2.imprint","IMPRINT",FACE,{"disambiguationData":[TD([[makeQuery(id+"F2.imprint","IMPRINT",EDGE,{"disambiguationData":[TD([[subQ2,-1.0]])],"derivedFrom":subQ1}),1.0]])]});}
            var Q56;
            {var subQ0=sQuery(id+"F2.wireOp",EDGE,"E26");var subQ1=sQuery(id+"F2.wireOp",EDGE,"E20");var subQ2=makeQuery(id+"F2.imprint","INTERSECT",VERTEX,{"derivedFrom":[subQ1,subQ0]});Q56=makeQuery(id+"F2.imprint","IMPRINT",FACE,{"disambiguationData":[TD([[makeQuery(id+"F2.imprint","IMPRINT",EDGE,{"disambiguationData":[TD([[subQ2,-1.0]])],"derivedFrom":subQ1}),1.0]])]});}
            var Q57;
            {var subQ0=sQuery(id+"F2.wireOp",EDGE,"E53");var subQ1=sQuery(id+"F2.wireOp",EDGE,"E20");var subQ2=makeQuery(id+"F2.imprint","INTERSECT",VERTEX,{"disambiguationData":[OD(0.0)],"derivedFrom":[subQ1,subQ0]});Q57=makeQuery(id+"F2.imprint","IMPRINT",FACE,{"disambiguationData":[TD([[makeQuery(id+"F2.imprint","IMPRINT",EDGE,{"disambiguationData":[TD([[subQ2,-1.0]])],"derivedFrom":subQ1}),1.0]])]});}
            var Q58;
            {var subQ0=sQuery(id+"F2.wireOp",EDGE,"E53");var subQ1=sQuery(id+"F2.wireOp",EDGE,"E20");var subQ2=makeQuery(id+"F2.imprint","INTERSECT",VERTEX,{"disambiguationData":[OD(0.0)],"derivedFrom":[subQ1,subQ0]});Q58=makeQuery(id+"F2.imprint","IMPRINT",FACE,{"disambiguationData":[TD([[makeQuery(id+"F2.imprint","IMPRINT",EDGE,{"disambiguationData":[TD([[subQ2,-1.0]])],"derivedFrom":subQ1}),-1.0]])]});}
            var Q59;
            {var subQ0=sQuery(id+"F2.wireOp",EDGE,"E26");var subQ1=sQuery(id+"F2.wireOp",EDGE,"E20");var subQ2=makeQuery(id+"F2.imprint","INTERSECT",VERTEX,{"derivedFrom":[subQ1,subQ0]});Q59=makeQuery(id+"F2.imprint","IMPRINT",FACE,{"disambiguationData":[TD([[makeQuery(id+"F2.imprint","IMPRINT",EDGE,{"disambiguationData":[TD([[subQ2,-1.0]])],"derivedFrom":subQ1}),-1.0]])]});}
            var Q60;
            {var subQ0=sQuery(id+"F2.wireOp",EDGE,"E54");var subQ1=sQuery(id+"F2.wireOp",EDGE,"E20");var subQ2=makeQuery(id+"F2.imprint","INTERSECT",VERTEX,{"disambiguationData":[OD(0.0)],"derivedFrom":[subQ1,subQ0]});Q60=makeQuery(id+"F2.imprint","IMPRINT",FACE,{"disambiguationData":[TD([[makeQuery(id+"F2.imprint","IMPRINT",EDGE,{"disambiguationData":[TD([[subQ2,-1.0]])],"derivedFrom":subQ1}),1.0]])]});}
            var Q61;
            {var subQ0=sQuery(id+"F2.wireOp",EDGE,"E28");var subQ1=sQuery(id+"F2.wireOp",EDGE,"E20");var subQ2=makeQuery(id+"F2.imprint","INTERSECT",VERTEX,{"derivedFrom":[subQ1,subQ0]});Q61=makeQuery(id+"F2.imprint","IMPRINT",FACE,{"disambiguationData":[TD([[makeQuery(id+"F2.imprint","IMPRINT",EDGE,{"disambiguationData":[TD([[subQ2,-1.0]])],"derivedFrom":subQ1}),1.0]])]});}
            var Q62;
            {var subQ0=sQuery(id+"F2.wireOp",EDGE,"E54");var subQ1=sQuery(id+"F2.wireOp",EDGE,"E20");var subQ2=makeQuery(id+"F2.imprint","INTERSECT",VERTEX,{"disambiguationData":[OD(0.0)],"derivedFrom":[subQ1,subQ0]});Q62=makeQuery(id+"F2.imprint","IMPRINT",FACE,{"disambiguationData":[TD([[makeQuery(id+"F2.imprint","IMPRINT",EDGE,{"disambiguationData":[TD([[subQ2,-1.0]])],"derivedFrom":subQ1}),-1.0]])]});}
            var Q63;
            {var subQ0=sQuery(id+"F2.wireOp",EDGE,"E28");var subQ1=sQuery(id+"F2.wireOp",EDGE,"E20");var subQ2=makeQuery(id+"F2.imprint","INTERSECT",VERTEX,{"derivedFrom":[subQ1,subQ0]});Q63=makeQuery(id+"F2.imprint","IMPRINT",FACE,{"disambiguationData":[TD([[makeQuery(id+"F2.imprint","IMPRINT",EDGE,{"disambiguationData":[TD([[subQ2,-1.0]])],"derivedFrom":subQ1}),-1.0]])]});}
            var Q64;
            {var subQ0=sQuery(id+"F2.wireOp",EDGE,"E55");var subQ1=sQuery(id+"F2.wireOp",EDGE,"E20");var subQ2=makeQuery(id+"F2.imprint","INTERSECT",VERTEX,{"disambiguationData":[OD(0.0)],"derivedFrom":[subQ1,subQ0]});Q64=makeQuery(id+"F2.imprint","IMPRINT",FACE,{"disambiguationData":[TD([[makeQuery(id+"F2.imprint","IMPRINT",EDGE,{"disambiguationData":[TD([[subQ2,-1.0]])],"derivedFrom":subQ1}),-1.0]])]});}
            var Q65;
            {var subQ0=sQuery(id+"F2.wireOp",EDGE,"E55");var subQ1=sQuery(id+"F2.wireOp",EDGE,"E20");var subQ2=makeQuery(id+"F2.imprint","INTERSECT",VERTEX,{"disambiguationData":[OD(0.0)],"derivedFrom":[subQ1,subQ0]});Q65=makeQuery(id+"F2.imprint","IMPRINT",FACE,{"disambiguationData":[TD([[makeQuery(id+"F2.imprint","IMPRINT",EDGE,{"disambiguationData":[TD([[subQ2,-1.0]])],"derivedFrom":subQ1}),1.0]])]});}
            var Q66;
            {var subQ0=sQuery(id+"F2.wireOp",EDGE,"E30");var subQ1=sQuery(id+"F2.wireOp",EDGE,"E20");var subQ2=makeQuery(id+"F2.imprint","INTERSECT",VERTEX,{"derivedFrom":[subQ1,subQ0]});Q66=makeQuery(id+"F2.imprint","IMPRINT",FACE,{"disambiguationData":[TD([[makeQuery(id+"F2.imprint","IMPRINT",EDGE,{"disambiguationData":[TD([[subQ2,-1.0]])],"derivedFrom":subQ1}),1.0]])]});}
            var Q67;
            {var subQ0=sQuery(id+"F2.wireOp",EDGE,"E30");var subQ1=sQuery(id+"F2.wireOp",EDGE,"E20");var subQ2=makeQuery(id+"F2.imprint","INTERSECT",VERTEX,{"derivedFrom":[subQ1,subQ0]});Q67=makeQuery(id+"F2.imprint","IMPRINT",FACE,{"disambiguationData":[TD([[makeQuery(id+"F2.imprint","IMPRINT",EDGE,{"disambiguationData":[TD([[subQ2,-1.0]])],"derivedFrom":subQ1}),-1.0]])]});}
            var Q68;
            {var subQ0=sQuery(id+"F2.wireOp",EDGE,"E56");var subQ1=sQuery(id+"F2.wireOp",EDGE,"E20");var subQ2=makeQuery(id+"F2.imprint","INTERSECT",VERTEX,{"disambiguationData":[OD(0.0)],"derivedFrom":[subQ1,subQ0]});Q68=makeQuery(id+"F2.imprint","IMPRINT",FACE,{"disambiguationData":[TD([[makeQuery(id+"F2.imprint","IMPRINT",EDGE,{"disambiguationData":[TD([[subQ2,-1.0]])],"derivedFrom":subQ1}),-1.0]])]});}
            var Q69;
            {var subQ0=sQuery(id+"F2.wireOp",EDGE,"E32");var subQ1=sQuery(id+"F2.wireOp",EDGE,"E20");var subQ2=makeQuery(id+"F2.imprint","INTERSECT",VERTEX,{"derivedFrom":[subQ1,subQ0]});Q69=makeQuery(id+"F2.imprint","IMPRINT",FACE,{"disambiguationData":[TD([[makeQuery(id+"F2.imprint","IMPRINT",EDGE,{"disambiguationData":[TD([[subQ2,-1.0]])],"derivedFrom":subQ1}),-1.0]])]});}
            var Q70;
            {var subQ0=sQuery(id+"F2.wireOp",EDGE,"E32");var subQ1=sQuery(id+"F2.wireOp",EDGE,"E20");var subQ2=makeQuery(id+"F2.imprint","INTERSECT",VERTEX,{"derivedFrom":[subQ1,subQ0]});Q70=makeQuery(id+"F2.imprint","IMPRINT",FACE,{"disambiguationData":[TD([[makeQuery(id+"F2.imprint","IMPRINT",EDGE,{"disambiguationData":[TD([[subQ2,-1.0]])],"derivedFrom":subQ1}),1.0]])]});}
            var Q71;
            {var subQ0=sQuery(id+"F2.wireOp",EDGE,"E56");var subQ1=sQuery(id+"F2.wireOp",EDGE,"E20");var subQ2=makeQuery(id+"F2.imprint","INTERSECT",VERTEX,{"disambiguationData":[OD(0.0)],"derivedFrom":[subQ1,subQ0]});Q71=makeQuery(id+"F2.imprint","IMPRINT",FACE,{"disambiguationData":[TD([[makeQuery(id+"F2.imprint","IMPRINT",EDGE,{"disambiguationData":[TD([[subQ2,-1.0]])],"derivedFrom":subQ1}),1.0]])]});}
            var Q72;
            {var subQ0=sQuery(id+"F2.wireOp",EDGE,"E51");var subQ1=sQuery(id+"F2.wireOp",EDGE,"E18");var subQ2=makeQuery(id+"F2.imprint","INTERSECT",VERTEX,{"disambiguationData":[OD(0.0)],"derivedFrom":[subQ1,subQ0]});Q72=makeQuery(id+"F2.imprint","IMPRINT",FACE,{"disambiguationData":[TD([[makeQuery(id+"F2.imprint","IMPRINT",EDGE,{"disambiguationData":[TD([[subQ2,-1.0]])],"derivedFrom":subQ1}),-1.0]])]});}
            var Q73;
            {var subQ0=sQuery(id+"F2.wireOp",EDGE,"E32");var subQ1=sQuery(id+"F2.wireOp",EDGE,"E18");var subQ2=makeQuery(id+"F2.imprint","INTERSECT",VERTEX,{"derivedFrom":[subQ1,subQ0]});Q73=makeQuery(id+"F2.imprint","IMPRINT",FACE,{"disambiguationData":[TD([[makeQuery(id+"F2.imprint","IMPRINT",EDGE,{"disambiguationData":[TD([[subQ2,-1.0]])],"derivedFrom":subQ1}),-1.0]])]});}
            var Q74;
            {var subQ0=sQuery(id+"F2.wireOp",EDGE,"E32");var subQ1=sQuery(id+"F2.wireOp",EDGE,"E18");var subQ2=makeQuery(id+"F2.imprint","INTERSECT",VERTEX,{"derivedFrom":[subQ1,subQ0]});Q74=makeQuery(id+"F2.imprint","IMPRINT",FACE,{"disambiguationData":[TD([[makeQuery(id+"F2.imprint","IMPRINT",EDGE,{"disambiguationData":[TD([[subQ2,-1.0]])],"derivedFrom":subQ1}),1.0]])]});}
            var Q75;
            {var subQ0=sQuery(id+"F2.wireOp",EDGE,"E51");var subQ1=sQuery(id+"F2.wireOp",EDGE,"E18");var subQ2=makeQuery(id+"F2.imprint","INTERSECT",VERTEX,{"disambiguationData":[OD(0.0)],"derivedFrom":[subQ1,subQ0]});Q75=makeQuery(id+"F2.imprint","IMPRINT",FACE,{"disambiguationData":[TD([[makeQuery(id+"F2.imprint","IMPRINT",EDGE,{"disambiguationData":[TD([[subQ2,-1.0]])],"derivedFrom":subQ1}),1.0]])]});}
            var Q76;
            {var subQ0=sQuery(id+"F2.wireOp",EDGE,"E30");var subQ1=sQuery(id+"F2.wireOp",EDGE,"E18");var subQ2=makeQuery(id+"F2.imprint","INTERSECT",VERTEX,{"derivedFrom":[subQ1,subQ0]});Q76=makeQuery(id+"F2.imprint","IMPRINT",FACE,{"disambiguationData":[TD([[makeQuery(id+"F2.imprint","IMPRINT",EDGE,{"disambiguationData":[TD([[subQ2,-1.0]])],"derivedFrom":subQ1}),1.0]])]});}
            var Q77;
            {var subQ0=sQuery(id+"F2.wireOp",EDGE,"E50");var subQ1=sQuery(id+"F2.wireOp",EDGE,"E18");var subQ2=makeQuery(id+"F2.imprint","INTERSECT",VERTEX,{"disambiguationData":[OD(0.0)],"derivedFrom":[subQ1,subQ0]});Q77=makeQuery(id+"F2.imprint","IMPRINT",FACE,{"disambiguationData":[TD([[makeQuery(id+"F2.imprint","IMPRINT",EDGE,{"disambiguationData":[TD([[subQ2,-1.0]])],"derivedFrom":subQ1}),1.0]])]});}
            var Q78;
            {var subQ0=sQuery(id+"F2.wireOp",EDGE,"E50");var subQ1=sQuery(id+"F2.wireOp",EDGE,"E18");var subQ2=makeQuery(id+"F2.imprint","INTERSECT",VERTEX,{"disambiguationData":[OD(0.0)],"derivedFrom":[subQ1,subQ0]});Q78=makeQuery(id+"F2.imprint","IMPRINT",FACE,{"disambiguationData":[TD([[makeQuery(id+"F2.imprint","IMPRINT",EDGE,{"disambiguationData":[TD([[subQ2,-1.0]])],"derivedFrom":subQ1}),-1.0]])]});}
            var Q79;
            {var subQ0=sQuery(id+"F2.wireOp",EDGE,"E30");var subQ1=sQuery(id+"F2.wireOp",EDGE,"E18");var subQ2=makeQuery(id+"F2.imprint","INTERSECT",VERTEX,{"derivedFrom":[subQ1,subQ0]});Q79=makeQuery(id+"F2.imprint","IMPRINT",FACE,{"disambiguationData":[TD([[makeQuery(id+"F2.imprint","IMPRINT",EDGE,{"disambiguationData":[TD([[subQ2,-1.0]])],"derivedFrom":subQ1}),-1.0]])]});}
            var Q80;
            {var subQ0=sQuery(id+"F2.wireOp",EDGE,"E45");var subQ1=sQuery(id+"F2.wireOp",EDGE,"E16");var subQ2=makeQuery(id+"F2.imprint","INTERSECT",VERTEX,{"disambiguationData":[OD(0.0)],"derivedFrom":[subQ1,subQ0]});Q80=makeQuery(id+"F2.imprint","IMPRINT",FACE,{"disambiguationData":[TD([[makeQuery(id+"F2.imprint","IMPRINT",EDGE,{"disambiguationData":[TD([[subQ2,-1.0]])],"derivedFrom":subQ1}),-1.0]])]});}
            var Q81;
            {var subQ0=sQuery(id+"F2.wireOp",EDGE,"E30");var subQ1=sQuery(id+"F2.wireOp",EDGE,"E16");var subQ2=makeQuery(id+"F2.imprint","INTERSECT",VERTEX,{"derivedFrom":[subQ1,subQ0]});Q81=makeQuery(id+"F2.imprint","IMPRINT",FACE,{"disambiguationData":[TD([[makeQuery(id+"F2.imprint","IMPRINT",EDGE,{"disambiguationData":[TD([[subQ2,-1.0]])],"derivedFrom":subQ1}),-1.0]])]});}
            var Q82;
            {var subQ0=sQuery(id+"F2.wireOp",EDGE,"E30");var subQ1=sQuery(id+"F2.wireOp",EDGE,"E16");var subQ2=makeQuery(id+"F2.imprint","INTERSECT",VERTEX,{"derivedFrom":[subQ1,subQ0]});Q82=makeQuery(id+"F2.imprint","IMPRINT",FACE,{"disambiguationData":[TD([[makeQuery(id+"F2.imprint","IMPRINT",EDGE,{"disambiguationData":[TD([[subQ2,-1.0]])],"derivedFrom":subQ1}),1.0]])]});}
            var Q83;
            {var subQ0=sQuery(id+"F2.wireOp",EDGE,"E45");var subQ1=sQuery(id+"F2.wireOp",EDGE,"E16");var subQ2=makeQuery(id+"F2.imprint","INTERSECT",VERTEX,{"disambiguationData":[OD(0.0)],"derivedFrom":[subQ1,subQ0]});Q83=makeQuery(id+"F2.imprint","IMPRINT",FACE,{"disambiguationData":[TD([[makeQuery(id+"F2.imprint","IMPRINT",EDGE,{"disambiguationData":[TD([[subQ2,-1.0]])],"derivedFrom":subQ1}),1.0]])]});}
            var Q84;
            {var subQ0=sQuery(id+"F2.wireOp",EDGE,"E46");var subQ1=sQuery(id+"F2.wireOp",EDGE,"E16");var subQ2=makeQuery(id+"F2.imprint","INTERSECT",VERTEX,{"disambiguationData":[OD(0.0)],"derivedFrom":[subQ1,subQ0]});Q84=makeQuery(id+"F2.imprint","IMPRINT",FACE,{"disambiguationData":[TD([[makeQuery(id+"F2.imprint","IMPRINT",EDGE,{"disambiguationData":[TD([[subQ2,-1.0]])],"derivedFrom":subQ1}),1.0]])]});}
            var Q85;
            {var subQ0=sQuery(id+"F2.wireOp",EDGE,"E32");var subQ1=sQuery(id+"F2.wireOp",EDGE,"E16");var subQ2=makeQuery(id+"F2.imprint","INTERSECT",VERTEX,{"derivedFrom":[subQ1,subQ0]});Q85=makeQuery(id+"F2.imprint","IMPRINT",FACE,{"disambiguationData":[TD([[makeQuery(id+"F2.imprint","IMPRINT",EDGE,{"disambiguationData":[TD([[subQ2,-1.0]])],"derivedFrom":subQ1}),1.0]])]});}
            var Q86;
            {var subQ0=sQuery(id+"F2.wireOp",EDGE,"E46");var subQ1=sQuery(id+"F2.wireOp",EDGE,"E16");var subQ2=makeQuery(id+"F2.imprint","INTERSECT",VERTEX,{"disambiguationData":[OD(0.0)],"derivedFrom":[subQ1,subQ0]});Q86=makeQuery(id+"F2.imprint","IMPRINT",FACE,{"disambiguationData":[TD([[makeQuery(id+"F2.imprint","IMPRINT",EDGE,{"disambiguationData":[TD([[subQ2,-1.0]])],"derivedFrom":subQ1}),-1.0]])]});}
            var Q87;
            {var subQ0=sQuery(id+"F2.wireOp",EDGE,"E32");var subQ1=sQuery(id+"F2.wireOp",EDGE,"E16");var subQ2=makeQuery(id+"F2.imprint","INTERSECT",VERTEX,{"derivedFrom":[subQ1,subQ0]});Q87=makeQuery(id+"F2.imprint","IMPRINT",FACE,{"disambiguationData":[TD([[makeQuery(id+"F2.imprint","IMPRINT",EDGE,{"disambiguationData":[TD([[subQ2,-1.0]])],"derivedFrom":subQ1}),-1.0]])]});}
            var Q88;
            {var subQ0=sQuery(id+"F2.wireOp",EDGE,"E30");var subQ1=sQuery(id+"F2.wireOp",EDGE,"E14");var subQ2=makeQuery(id+"F2.imprint","INTERSECT",VERTEX,{"derivedFrom":[subQ1,subQ0]});Q88=makeQuery(id+"F2.imprint","IMPRINT",FACE,{"disambiguationData":[TD([[makeQuery(id+"F2.imprint","IMPRINT",EDGE,{"disambiguationData":[TD([[subQ2,-1.0]])],"derivedFrom":subQ1}),-1.0]])]});}
            var Q89;
            {var subQ0=sQuery(id+"F2.wireOp",EDGE,"E40");var subQ1=sQuery(id+"F2.wireOp",EDGE,"E14");var subQ2=makeQuery(id+"F2.imprint","INTERSECT",VERTEX,{"disambiguationData":[OD(0.0)],"derivedFrom":[subQ1,subQ0]});Q89=makeQuery(id+"F2.imprint","IMPRINT",FACE,{"disambiguationData":[TD([[makeQuery(id+"F2.imprint","IMPRINT",EDGE,{"disambiguationData":[TD([[subQ2,-1.0]])],"derivedFrom":subQ1}),-1.0]])]});}
            var Q90;
            {var subQ0=sQuery(id+"F2.wireOp",EDGE,"E40");var subQ1=sQuery(id+"F2.wireOp",EDGE,"E14");var subQ2=makeQuery(id+"F2.imprint","INTERSECT",VERTEX,{"disambiguationData":[OD(0.0)],"derivedFrom":[subQ1,subQ0]});Q90=makeQuery(id+"F2.imprint","IMPRINT",FACE,{"disambiguationData":[TD([[makeQuery(id+"F2.imprint","IMPRINT",EDGE,{"disambiguationData":[TD([[subQ2,-1.0]])],"derivedFrom":subQ1}),1.0]])]});}
            var Q91;
            {var subQ0=sQuery(id+"F2.wireOp",EDGE,"E30");var subQ1=sQuery(id+"F2.wireOp",EDGE,"E14");var subQ2=makeQuery(id+"F2.imprint","INTERSECT",VERTEX,{"derivedFrom":[subQ1,subQ0]});Q91=makeQuery(id+"F2.imprint","IMPRINT",FACE,{"disambiguationData":[TD([[makeQuery(id+"F2.imprint","IMPRINT",EDGE,{"disambiguationData":[TD([[subQ2,-1.0]])],"derivedFrom":subQ1}),1.0]])]});}
            var Q92;
            {var subQ0=sQuery(id+"F2.wireOp",EDGE,"E41");var subQ1=sQuery(id+"F2.wireOp",EDGE,"E14");var subQ2=makeQuery(id+"F2.imprint","INTERSECT",VERTEX,{"disambiguationData":[OD(0.0)],"derivedFrom":[subQ1,subQ0]});Q92=makeQuery(id+"F2.imprint","IMPRINT",FACE,{"disambiguationData":[TD([[makeQuery(id+"F2.imprint","IMPRINT",EDGE,{"disambiguationData":[TD([[subQ2,-1.0]])],"derivedFrom":subQ1}),1.0]])]});}
            var Q93;
            {var subQ0=sQuery(id+"F2.wireOp",EDGE,"E32");var subQ1=sQuery(id+"F2.wireOp",EDGE,"E14");var subQ2=makeQuery(id+"F2.imprint","INTERSECT",VERTEX,{"derivedFrom":[subQ1,subQ0]});Q93=makeQuery(id+"F2.imprint","IMPRINT",FACE,{"disambiguationData":[TD([[makeQuery(id+"F2.imprint","IMPRINT",EDGE,{"disambiguationData":[TD([[subQ2,-1.0]])],"derivedFrom":subQ1}),1.0]])]});}
            var Q94;
            {var subQ0=sQuery(id+"F2.wireOp",EDGE,"E41");var subQ1=sQuery(id+"F2.wireOp",EDGE,"E14");var subQ2=makeQuery(id+"F2.imprint","INTERSECT",VERTEX,{"disambiguationData":[OD(0.0)],"derivedFrom":[subQ1,subQ0]});Q94=makeQuery(id+"F2.imprint","IMPRINT",FACE,{"disambiguationData":[TD([[makeQuery(id+"F2.imprint","IMPRINT",EDGE,{"disambiguationData":[TD([[subQ2,-1.0]])],"derivedFrom":subQ1}),-1.0]])]});}
            var Q95;
            {var subQ0=sQuery(id+"F2.wireOp",EDGE,"E32");var subQ1=sQuery(id+"F2.wireOp",EDGE,"E14");var subQ2=makeQuery(id+"F2.imprint","INTERSECT",VERTEX,{"derivedFrom":[subQ1,subQ0]});Q95=makeQuery(id+"F2.imprint","IMPRINT",FACE,{"disambiguationData":[TD([[makeQuery(id+"F2.imprint","IMPRINT",EDGE,{"disambiguationData":[TD([[subQ2,-1.0]])],"derivedFrom":subQ1}),-1.0]])]});}
            var Q96;
            Q96=makeQuery(id+"F2.imprint","IMPRINT",FACE,{"disambiguationData":[TD([[makeQuery(id+"F2.imprint","IMPRINT",EDGE,{"derivedFrom":sQuery(id+"F2.wireOp",EDGE,"E60")}),1.0]])]});
            var Q97;
            Q97=sQuery(id+"F2.wireOp",EDGE,"E36");
            var Q98;
            Q98=sQuery(id+"F2.wireOp",EDGE,"E37");
            var Q99;
            Q99=sQuery(id+"F2.wireOp",EDGE,"E38");
            var Q100;
            Q100=sQuery(id+"F2.wireOp",EDGE,"E39");
            var Q101;
            Q101=sQuery(id+"F2.wireOp",EDGE,"E40");
            var Q102;
            Q102=sQuery(id+"F2.wireOp",EDGE,"E41");
            var Q103;
            Q103=sQuery(id+"F2.wireOp",EDGE,"E57");
            var Q104;
            Q104=sQuery(id+"F2.wireOp",EDGE,"E42");
            var Q105;
            Q105=sQuery(id+"F2.wireOp",EDGE,"E43");
            var Q106;
            Q106=sQuery(id+"F2.wireOp",EDGE,"E44");
            var Q107;
            Q107=sQuery(id+"F2.wireOp",EDGE,"E45");
            var Q108;
            Q108=sQuery(id+"F2.wireOp",EDGE,"E46");
            var Q109;
            Q109=sQuery(id+"F2.wireOp",EDGE,"E51");
            var Q110;
            Q110=sQuery(id+"F2.wireOp",EDGE,"E50");
            var Q111;
            Q111=sQuery(id+"F2.wireOp",EDGE,"E56");
            var Q112;
            Q112=sQuery(id+"F2.wireOp",EDGE,"E55");
            var Q113;
            Q113=sQuery(id+"F2.wireOp",EDGE,"E49");
            var Q114;
            Q114=sQuery(id+"F2.wireOp",EDGE,"E54");
            var Q115;
            Q115=sQuery(id+"F2.wireOp",EDGE,"E53");
            var Q116;
            Q116=sQuery(id+"F2.wireOp",EDGE,"E48");
            var Q117;
            Q117=sQuery(id+"F2.wireOp",EDGE,"E47");
            var Q118;
            Q118=sQuery(id+"F2.wireOp",EDGE,"E52");
            var Q119;
            Q119=sQuery(id+"F2.wireOp",EDGE,"E59");
            var Q120;
            Q120=sQuery(id+"F2.wireOp",EDGE,"E58");
            extrude(context, id + "F3", {"entities" : qUnion([Q0, Q1, Q2, Q3, Q4, Q5, Q6, Q7, Q8, Q9, Q10, Q11, Q12, Q13, Q14, Q15, Q16, Q17, Q18, Q19, Q20, Q21, Q22, Q23, Q24, Q25, Q26, Q27, Q28, Q29, Q30, Q31, Q32, Q33, Q34, Q35, Q36, Q37, Q38, Q39, Q40, Q41, Q42, Q43, Q44, Q45, Q46, Q47, Q48, Q49, Q50, Q51, Q52, Q53, Q54, Q55, Q56, Q57, Q58, Q59, Q60, Q61, Q62, Q63, Q64, Q65, Q66, Q67, Q68, Q69, Q70, Q71, Q72, Q73, Q74, Q75, Q76, Q77, Q78, Q79, Q80, Q81, Q82, Q83, Q84, Q85, Q86, Q87, Q88, Q89, Q90, Q91, Q92, Q93, Q94, Q95, Q96]), "operationType" : NewBodyOperationType.REMOVE, "surfaceEntities" : qUnion([Q97, Q98, Q99, Q100, Q101, Q102, Q103, Q104, Q105, Q106, Q107, Q108, Q109, Q110, Q111, Q112, Q113, Q114, Q115, Q116, Q117, Q118, Q119, Q120]), "oppositeDirection" : true, "depth" : 17.4 * mm, "offsetDistance" : 25 * mm});
        }
    });
